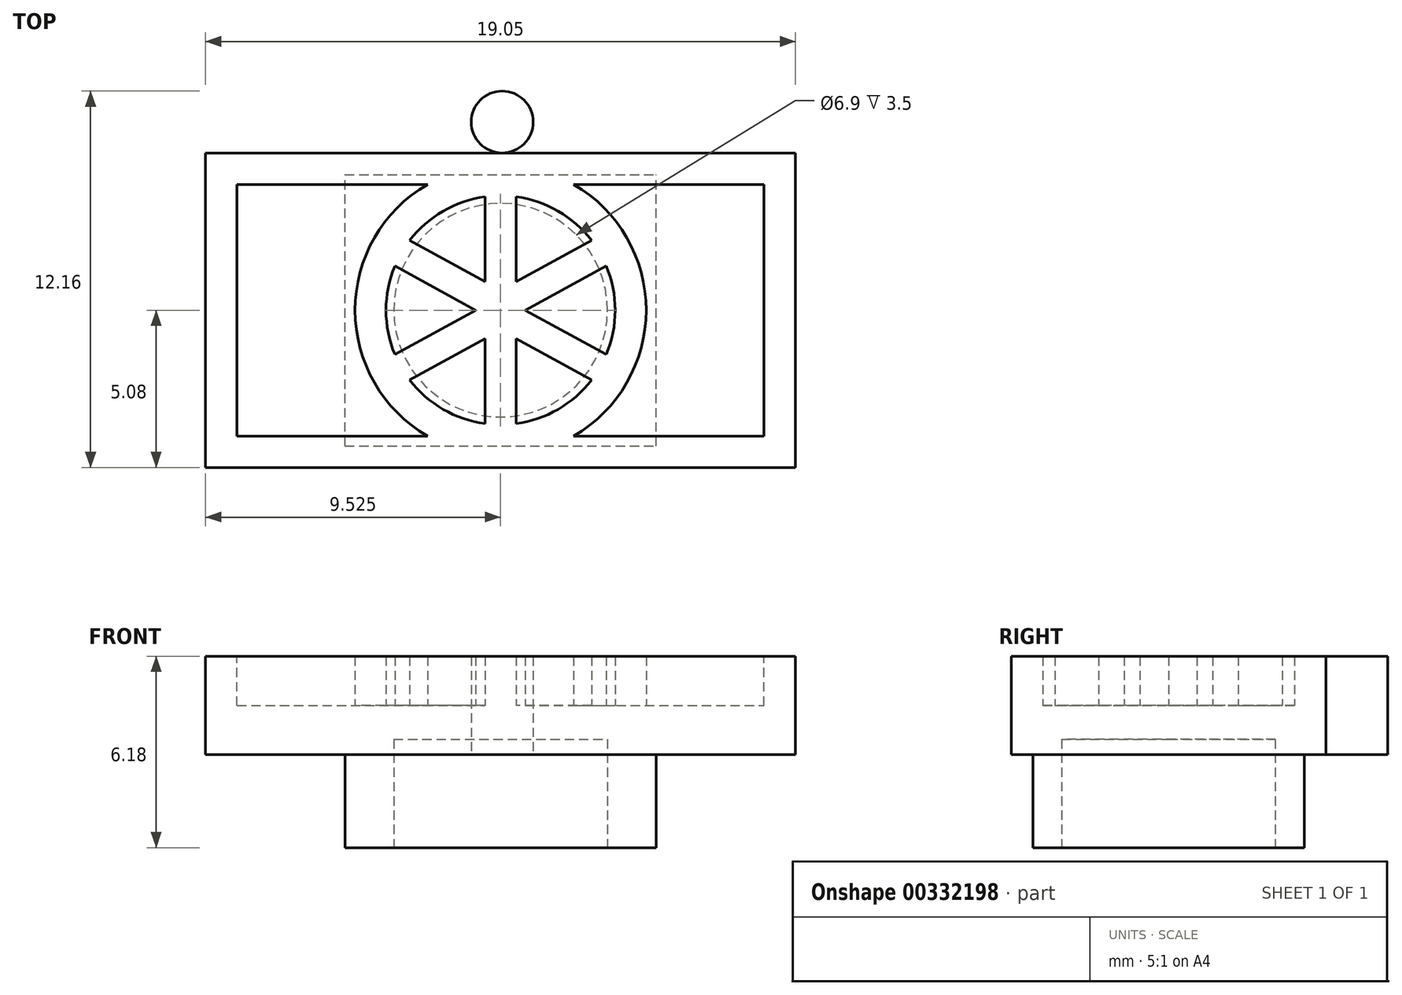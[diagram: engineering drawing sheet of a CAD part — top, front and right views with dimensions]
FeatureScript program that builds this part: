
annotation { "Feature Type Name" : "Feature", "Feature Type Description" : "" }
export const myFeature = defineFeature(function(context is Context, id is Id, definition is map)
    precondition{}
    {
        {
            var Q0;
            Q0=qCreatedBy(makeId("Top.planeOp"),FACE);
            var sketch = newSketch(context, id + "F0", { "sketchPlane" : qUnion([Q0])});
            skLineSegment(sketch, "E0.bottom", {"start": v(-19.05, 10.16) * mm, "end": v(0, 10.16) * mm});
            skLineSegment(sketch, "E0.top", {"start": v(-19.05, 0) * mm, "end": v(0, 0) * mm});
            skLineSegment(sketch, "E0.left", {"start": v(-19.05, 10.16) * mm, "end": v(-19.05, 0) * mm});
            skLineSegment(sketch, "E0.right", {"start": v(0, 10.16) * mm, "end": v(0, 0) * mm});
            skLineSegment(sketch, "E1", {"start": v(-9.52, 10.16) * mm, "end": v(-9.52, 0) * mm, "construction": true});
            skCircle(sketch, "E2", {"center": v(-9.48, 11.16) * mm, "radius": 1 * mm});
            skSolve(sketch);
        }
        {
            var Q0;
            Q0=qSketchRegion(id+"F0",true);
            extrude(context, id + "F1", {"entities" : qUnion([Q0]), "depth" : 3.17 * mm});
        }
        {
            var Q0;
            Q0=makeQuery(id+"F1.opExtrude","CAP_FACE",FACE,{"disambiguationData":[OSD([sQuery(id+"F0.wireOp",EDGE,"E0.bottom"),sQuery(id+"F0.wireOp",EDGE,"E0.top"),sQuery(id+"F0.wireOp",EDGE,"E0.left"),sQuery(id+"F0.wireOp",EDGE,"E0.right")])],"isStart":false});
            var sketch = newSketch(context, id + "F2", { "sketchPlane" : qUnion([Q0])});
            skLineSegment(sketch, "E3.bottom", {"start": v(-18.03, 9.14) * mm, "end": v(-1.02, 9.14) * mm});
            skLineSegment(sketch, "E3.top", {"start": v(-18.03, 1.02) * mm, "end": v(-1.02, 1.02) * mm});
            skLineSegment(sketch, "E3.left", {"start": v(-18.03, 9.14) * mm, "end": v(-18.03, 1.02) * mm});
            skLineSegment(sketch, "E3.right", {"start": v(-1.02, 9.14) * mm, "end": v(-1.02, 1.02) * mm});
            skSolve(sketch);
        }
        {
            var Q0;
            Q0=qSketchRegion(id+"F2",true);
            extrude(context, id + "F3", {"entities" : qUnion([Q0]), "operationType" : NewBodyOperationType.REMOVE, "oppositeDirection" : true, "depth" : 1.59 * mm});
        }
        {
            var Q0;
            {var subQ1=sQuery(id+"F2.wireOp",EDGE,"E3.top");var subQ4=makeQuery(id+"F3.boolean.opBoolean","COPY",FACE,{"derivedFrom":makeQuery(id+"F3.opExtrude","SWEPT_FACE",FACE,{"disambiguationData":[OSD([subQ1])]})});var subQ6=sQuery(id+"F2.wireOp",EDGE,"E3.right");Q0=makeQuery(id+"FbiU5rRMadnEj1Y_1.boolean.opBoolean","SPLIT",FACE,{"disambiguationData":[TD([subQ4])],"derivedFrom":makeQuery(id+"FD6hazfNaiJcgqe_1.boolean.opBoolean","SPLIT",FACE,{"disambiguationData":[TD([subQ4])],"derivedFrom":makeQuery(id+"F3.boolean.opBoolean","COPY",FACE,{"derivedFrom":makeQuery(id+"F3.opExtrude","CAP_FACE",FACE,{"disambiguationData":[OSD([sQuery(id+"F2.wireOp",EDGE,"E3.bottom"),subQ1,sQuery(id+"F2.wireOp",EDGE,"E3.left"),subQ6])],"isStart":false})})})});}
            var sketch = newSketch(context, id + "F4", { "sketchPlane" : qUnion([Q0])});
            skLineSegment(sketch, "E4", {"start": v(-19.05, 1.68) * mm, "end": v(-1.02, 1.68) * mm, "construction": true});
            skLineSegment(sketch, "E5", {"start": v(-9.53, 10.16) * mm, "end": v(-9.53, 0) * mm, "construction": true});
            skSolve(sketch);
        }
        {
            var Q0;
            Q0=makeQuery(id+"F1.opExtrude","CAP_FACE",FACE,{"disambiguationData":[OSD([sQuery(id+"F0.wireOp",EDGE,"E0.bottom"),sQuery(id+"F0.wireOp",EDGE,"E0.top"),sQuery(id+"F0.wireOp",EDGE,"E0.left"),sQuery(id+"F0.wireOp",EDGE,"E0.right"),sQuery(id+"F0.wireOp",EDGE,"iD4YVwzi-38ZZ-sZow-cuPB-LK5aPxXRs2tg"),sQuery(id+"F0.wireOp",EDGE,"25aa8db4-dd9b-41d2-b8c9-1594e9b75191"),sQuery(id+"F0.wireOp",EDGE,"40f63cb3-13d8-4821-a3c4-c05e674bd89b0.MirrorC")])],"isStart":true});
            var sketch = newSketch(context, id + "F5", { "sketchPlane" : qUnion([Q0])});
            skLineSegment(sketch, "E6.bottom", {"start": v(-14.55, -0.7) * mm, "end": v(-4.5, -0.7) * mm});
            skLineSegment(sketch, "E6.top", {"start": v(-14.55, -9.46) * mm, "end": v(-4.5, -9.46) * mm});
            skLineSegment(sketch, "E6.left", {"start": v(-14.55, -0.7) * mm, "end": v(-14.55, -9.46) * mm});
            skLineSegment(sketch, "E6.right", {"start": v(-4.5, -0.7) * mm, "end": v(-4.5, -9.46) * mm});
            skSolve(sketch);
        }
        {
            var Q0;
            Q0=qSketchRegion(id+"F5",true);
            extrude(context, id + "F6", {"entities" : qUnion([Q0]), "operationType" : NewBodyOperationType.ADD, "depth" : 3 * mm, "offsetDistance" : 25 * mm});
        }
        {
            var Q0;
            Q0=makeQuery(id+"F6.opExtrude","CAP_FACE",FACE,{"disambiguationData":[OSD([sQuery(id+"F5.wireOp",EDGE,"E6.bottom"),sQuery(id+"F5.wireOp",EDGE,"E6.top"),sQuery(id+"F5.wireOp",EDGE,"E6.left"),sQuery(id+"F5.wireOp",EDGE,"E6.right")])],"isStart":false});
            var sketch = newSketch(context, id + "F7", { "sketchPlane" : qUnion([Q0])});
            skCircle(sketch, "E7", {"center": v(-9.52, -5.08) * mm, "radius": 3.45 * mm});
            skLineSegment(sketch, "E8", {"start": v(-19.05, -5.08) * mm, "end": v(0, -5.08) * mm, "construction": true});
            skPoint(sketch, "E8.endSnap0", {"position": v(-4.5, -5.08) * mm});
            skLineSegment(sketch, "E9", {"start": v(-9.53, 0) * mm, "end": v(-9.53, -9.46) * mm, "construction": true});
            skSolve(sketch);
        }
        {
            var Q0;
            Q0=makeQuery(id+"F7.imprint","IMPRINT",FACE,{"disambiguationData":[TD([[makeQuery(id+"F7.imprint","IMPRINT",EDGE,{"derivedFrom":sQuery(id+"F7.wireOp",EDGE,"E7")}),1.0]])]});
            extrude(context, id + "F8", {"entities" : qUnion([Q0]), "operationType" : NewBodyOperationType.REMOVE, "oppositeDirection" : true, "depth" : 3.5 * mm, "offsetDistance" : 25 * mm});
        }
        {
            var Q0;
            Q0=makeQuery(id+"F4.imprint","IMPRINT",FACE,{"disambiguationData":[TD([[makeQuery(id+"F4.imprint","IMPRINT",EDGE,{"derivedFrom":makeQuery(id+"F3.boolean.opBoolean","COPY",EDGE,{"derivedFrom":makeQuery(id+"F3.opExtrude","CAP_EDGE",EDGE,{"disambiguationData":[OSD([sQuery(id+"F2.wireOp",EDGE,"E3.bottom")])],"isStart":false})})}),-1.0]])]});
            var sketch = newSketch(context, id + "F9", { "sketchPlane" : qUnion([Q0])});
            skLineSegment(sketch, "E10", {"start": v(-6.24, 7.53) * mm, "end": v(-9.53, 5.73) * mm});
            skLineSegment(sketch, "E11", {"start": v(-8.73, 5.08) * mm, "end": v(-5.54, 6.83) * mm});
            skLineSegment(sketch, "E12", {"start": v(-5.54, 6.83) * mm, "end": v(-5.54, 7.53) * mm});
            skLineSegment(sketch, "E13", {"start": v(-5.54, 7.53) * mm, "end": v(-6.24, 7.53) * mm});
            skLineSegment(sketch, "E14", {"start": v(-19.05, 5.08) * mm, "end": v(0, 5.08) * mm, "construction": true});
            skLineSegment(sketch, "E15.MirrorCS", {"start": v(-12.81, 7.53) * mm, "end": v(-9.53, 5.73) * mm});
            skLineSegment(sketch, "E16.MirrorCS", {"start": v(-10.33, 5.08) * mm, "end": v(-13.51, 6.83) * mm});
            skLineSegment(sketch, "E17.MirrorCS", {"start": v(-13.51, 6.83) * mm, "end": v(-13.51, 7.53) * mm});
            skLineSegment(sketch, "E18.MirrorCS", {"start": v(-13.51, 7.53) * mm, "end": v(-12.81, 7.53) * mm});
            skLineSegment(sketch, "E19.MirrorCS", {"start": v(-10.32, 5.08) * mm, "end": v(-13.51, 3.33) * mm});
            skLineSegment(sketch, "E20.MirrorCS", {"start": v(-8.72, 5.08) * mm, "end": v(-5.54, 3.33) * mm});
            skLineSegment(sketch, "E21.MirrorCS", {"start": v(-6.24, 2.63) * mm, "end": v(-9.53, 4.43) * mm});
            skLineSegment(sketch, "E22.MirrorCS", {"start": v(-12.81, 2.63) * mm, "end": v(-9.53, 4.43) * mm});
            skLineSegment(sketch, "E23.MirrorCS", {"start": v(-13.51, 2.63) * mm, "end": v(-12.81, 2.63) * mm});
            skLineSegment(sketch, "E24.MirrorCS", {"start": v(-13.51, 3.33) * mm, "end": v(-13.51, 2.63) * mm});
            skLineSegment(sketch, "E25.MirrorCS", {"start": v(-5.54, 3.33) * mm, "end": v(-5.54, 2.63) * mm});
            skLineSegment(sketch, "E26.MirrorCS", {"start": v(-5.54, 2.63) * mm, "end": v(-6.24, 2.63) * mm});
            skLineSegment(sketch, "E27.bottom", {"start": v(-10.03, 9.14) * mm, "end": v(-9.03, 9.14) * mm});
            skLineSegment(sketch, "E27.top", {"start": v(-10.03, 1.02) * mm, "end": v(-9.03, 1.02) * mm});
            skLineSegment(sketch, "E27.left", {"start": v(-10.03, 9.14) * mm, "end": v(-10.03, 1.02) * mm});
            skLineSegment(sketch, "E27.right", {"start": v(-9.03, 9.14) * mm, "end": v(-9.03, 1.02) * mm});
            skSolve(sketch);
        }
        {
            var Q0;
            Q0=qSketchRegion(id+"F9",true);
            var Q1;
            Q1=makeQuery(id+"FXsS83p9KQ4uv0L_1.boolean.opBoolean","MERGE",FACE,{"derivedFrom":[makeQuery(id+"F1.opExtrude","CAP_FACE",FACE,{"disambiguationData":[OSD([sQuery(id+"F0.wireOp",EDGE,"E0.bottom"),sQuery(id+"F0.wireOp",EDGE,"E0.top"),sQuery(id+"F0.wireOp",EDGE,"E0.left"),sQuery(id+"F0.wireOp",EDGE,"E0.right"),sQuery(id+"F0.wireOp",EDGE,"25aa8db4-dd9b-41d2-b8c9-1594e9b75191"),sQuery(id+"F0.wireOp",EDGE,"40f63cb3-13d8-4821-a3c4-c05e674bd89b0.MirrorC")])],"isStart":false}),makeQuery(id+"FbiU5rRMadnEj1Y_1.opExtrude","CAP_FACE",FACE,{"disambiguationData":[OSD([sQuery(id+"FmV1InaubWQgJeV_1.wireOp",EDGE,"lTleeF4S-0pnc-dI25-KJAR-2TLCTf0jWGc3"),sQuery(id+"FmV1InaubWQgJeV_1.wireOp",EDGE,"m9JDErra-axgF-Q1Zk-CJc0-x6RwavRCbCz8")])],"isStart":false}),makeQuery(id+"FXsS83p9KQ4uv0L_1.opExtrude","CAP_FACE",FACE,{"disambiguationData":[OSD([sQuery(id+"Fi3yzKCDt9pSW51_1.wireOp",EDGE,"cutzoVbR-JFbv-1kZ0-SQrw-pSLFGMZcN76v"),sQuery(id+"Fi3yzKCDt9pSW51_1.wireOp",EDGE,"XYQyWRLz-35l4-wHee-0FsY-Oat0KQk3jhR6"),sQuery(id+"Fi3yzKCDt9pSW51_1.wireOp",EDGE,"lBgadLLx-aQS8-kMAZ-d5qN-Zo8duSUxtBeX"),sQuery(id+"Fi3yzKCDt9pSW51_1.wireOp",EDGE,"DlRPRQGx-Alaq-SPUL-URFH-jddu6C2Nnp9z"),sQuery(id+"Fi3yzKCDt9pSW51_1.wireOp",EDGE,"Shc4e2eY-gIsf-lYKj-D0sO-212MCfLGw1w2"),sQuery(id+"Fi3yzKCDt9pSW51_1.wireOp",EDGE,"DXv1RSob-CDWK-uPmN-nh2c-bdjhB3yjVnB2"),sQuery(id+"Fi3yzKCDt9pSW51_1.wireOp",EDGE,"Mjf90MPI-7UZW-OfA1-fD3l-TGEU1IJ1uaYu"),sQuery(id+"Fi3yzKCDt9pSW51_1.wireOp",EDGE,"IrneLFi4-a4Xm-RgwH-oJvY-WcCPALNDAReP"),sQuery(id+"Fi3yzKCDt9pSW51_1.wireOp",EDGE,"toQdHavX-h7D1-dxbV-IXrh-P84p4AImceJh"),sQuery(id+"Fi3yzKCDt9pSW51_1.wireOp",EDGE,"xGw8HYbu-oKFY-4S3u-lNNy-w4TfAhwJFqQu"),sQuery(id+"Fi3yzKCDt9pSW51_1.wireOp",EDGE,"5pvZd2gl-M8UA-9HNZ-daD7-4TEjzgTyMgsA"),sQuery(id+"Fi3yzKCDt9pSW51_1.wireOp",EDGE,"b1702624-0c59-4015-bc2e-a5f6b81265a70.MirrorCS"),sQuery(id+"Fi3yzKCDt9pSW51_1.wireOp",EDGE,"7deeccc9-7886-4666-b44c-47b900ed28990.MirrorCS"),sQuery(id+"Fi3yzKCDt9pSW51_1.wireOp",EDGE,"75936777-967d-44d6-aacf-753113c8b50b0.MirrorCS"),sQuery(id+"Fi3yzKCDt9pSW51_1.wireOp",EDGE,"e5875930-5b2f-47d0-b261-f87a419dd3ea0.MirrorCS"),sQuery(id+"Fi3yzKCDt9pSW51_1.wireOp",EDGE,"e1f8200d-9078-41b5-85b4-8a4adb8dc9e80.MirrorCS"),sQuery(id+"Fi3yzKCDt9pSW51_1.wireOp",EDGE,"40fd4d9e-f758-4b42-b7b5-3e08d0cf58f50.MirrorCS"),sQuery(id+"Fi3yzKCDt9pSW51_1.wireOp",EDGE,"553d3a6c-e9a7-4b40-b1d3-0817f640e5cc0.MirrorCS"),sQuery(id+"Fi3yzKCDt9pSW51_1.wireOp",EDGE,"5a723a2c-c48e-43ea-a32e-a11b15ff1a7b0.MirrorCS"),sQuery(id+"Fi3yzKCDt9pSW51_1.wireOp",EDGE,"932d58c0-4b54-410d-a467-0e9cf49887c90.MirrorCS"),sQuery(id+"Fi3yzKCDt9pSW51_1.wireOp",EDGE,"eeedfdb4-aa26-4e83-bf33-b18388155c4d0.MirrorCS"),sQuery(id+"Fi3yzKCDt9pSW51_1.wireOp",EDGE,"a4c71cba-da55-4cc9-80cf-8947727491d80.MirrorCS")])],"isStart":false})]});
            extrude(context, id + "F10", {"entities" : qUnion([Q0]), "operationType" : NewBodyOperationType.ADD, "endBound" : BoundingType.UP_TO_SURFACE, "depth" : 25 * mm, "endBoundEntityFace" : qUnion([Q1]), "offsetDistance" : 25 * mm});
        }
        {
            var Q0;
            Q0=makeQuery(id+"F4.imprint","IMPRINT",FACE,{"disambiguationData":[TD([[makeQuery(id+"F4.imprint","IMPRINT",EDGE,{"derivedFrom":makeQuery(id+"F3.boolean.opBoolean","COPY",EDGE,{"derivedFrom":makeQuery(id+"F3.opExtrude","CAP_EDGE",EDGE,{"disambiguationData":[OSD([sQuery(id+"F2.wireOp",EDGE,"E3.bottom")])],"isStart":false})})}),-1.0]])]});
            var sketch = newSketch(context, id + "F11", { "sketchPlane" : qUnion([Q0])});
            skCircle(sketch, "E28", {"center": v(-9.53, 5.08) * mm, "radius": 3.7 * mm});
            skCircle(sketch, "E29", {"center": v(-9.53, 5.08) * mm, "radius": 4.7 * mm});
            skSolve(sketch);
        }
        {
            var Q0;
            Q0=qSketchRegion(id+"F11",true);
            var Q1;
            Q1=makeQuery(id+"F10.boolean.opBoolean","MERGE",FACE,{"derivedFrom":[makeQuery(id+"F1.opExtrude","CAP_FACE",FACE,{"disambiguationData":[OSD([sQuery(id+"F0.wireOp",EDGE,"E0.bottom"),sQuery(id+"F0.wireOp",EDGE,"E0.top"),sQuery(id+"F0.wireOp",EDGE,"E0.left"),sQuery(id+"F0.wireOp",EDGE,"E0.right")])],"isStart":false}),makeQuery(id+"F10.opExtrude","CAP_FACE",FACE,{"disambiguationData":[OSD([sQuery(id+"F9.wireOp",EDGE,"E10"),sQuery(id+"F9.wireOp",EDGE,"E11"),sQuery(id+"F9.wireOp",EDGE,"E12"),sQuery(id+"F9.wireOp",EDGE,"E13"),sQuery(id+"F9.wireOp",EDGE,"E15.MirrorCS"),sQuery(id+"F9.wireOp",EDGE,"E16.MirrorCS"),sQuery(id+"F9.wireOp",EDGE,"E17.MirrorCS"),sQuery(id+"F9.wireOp",EDGE,"E18.MirrorCS"),sQuery(id+"F9.wireOp",EDGE,"E19.MirrorCS"),sQuery(id+"F9.wireOp",EDGE,"E20.MirrorCS"),sQuery(id+"F9.wireOp",EDGE,"E21.MirrorCS"),sQuery(id+"F9.wireOp",EDGE,"E22.MirrorCS"),sQuery(id+"F9.wireOp",EDGE,"E23.MirrorCS"),sQuery(id+"F9.wireOp",EDGE,"E24.MirrorCS"),sQuery(id+"F9.wireOp",EDGE,"E25.MirrorCS"),sQuery(id+"F9.wireOp",EDGE,"E26.MirrorCS"),sQuery(id+"F9.wireOp",EDGE,"E27.bottom"),sQuery(id+"F9.wireOp",EDGE,"E27.top"),sQuery(id+"F9.wireOp",EDGE,"E27.left"),sQuery(id+"F9.wireOp",EDGE,"E27.right")])],"isStart":false})]});
            extrude(context, id + "F12", {"entities" : qUnion([Q0]), "operationType" : NewBodyOperationType.ADD, "endBound" : BoundingType.UP_TO_SURFACE, "depth" : 25 * mm, "endBoundEntityFace" : qUnion([Q1]), "offsetDistance" : 25 * mm});
        }
    });
